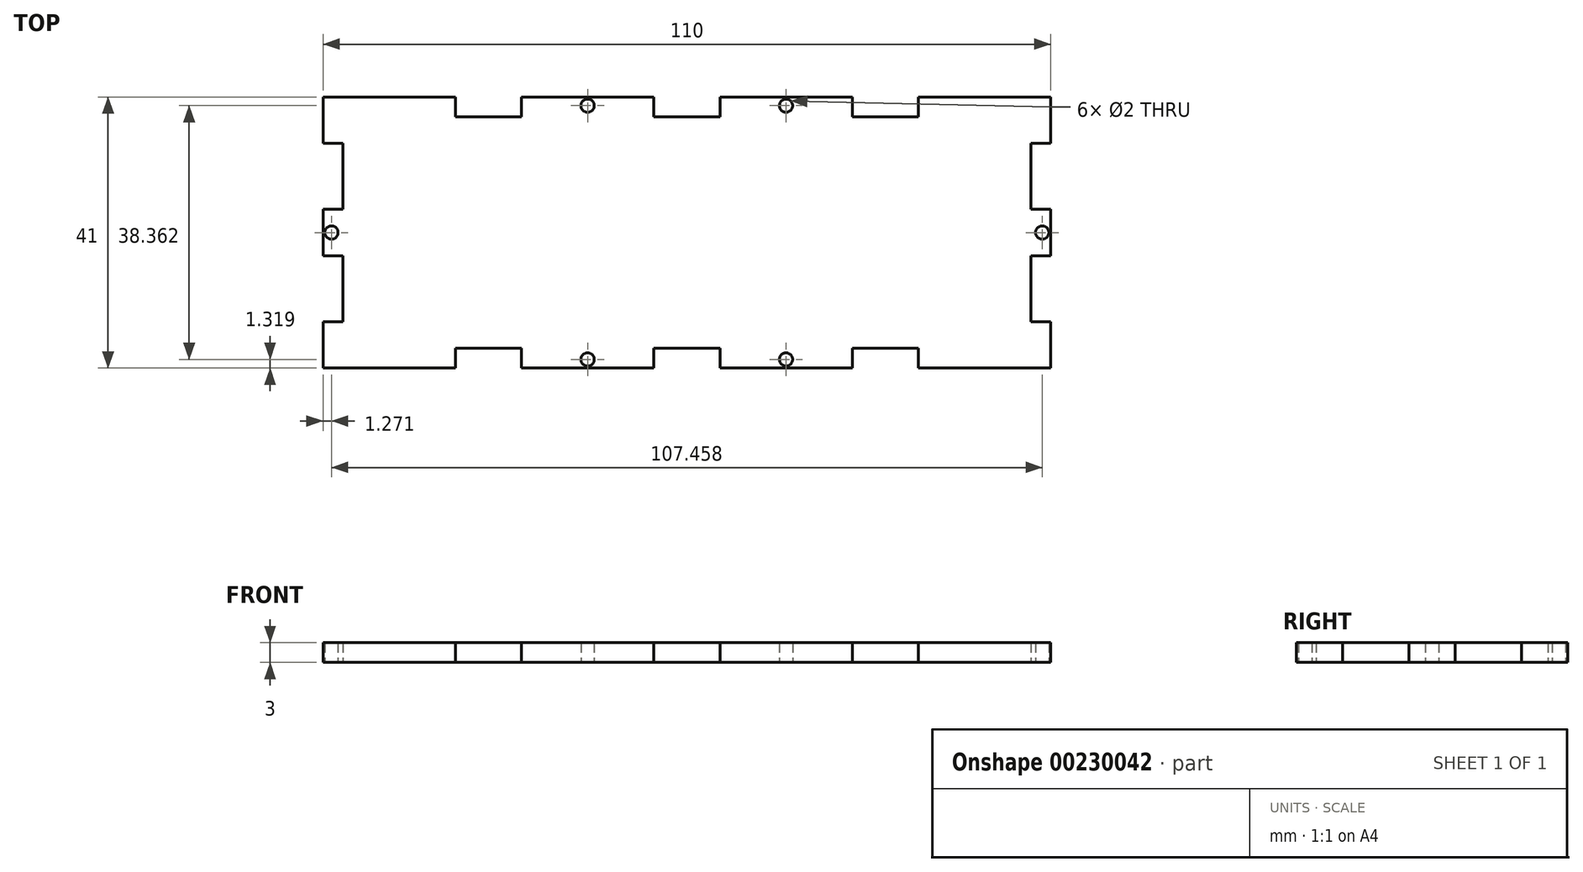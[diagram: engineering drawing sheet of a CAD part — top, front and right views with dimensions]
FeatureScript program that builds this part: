
annotation { "Feature Type Name" : "Feature", "Feature Type Description" : "" }
export const myFeature = defineFeature(function(context is Context, id is Id, definition is map)
    precondition{}
    {
        {
            var Q0;
            Q0=qCreatedBy(makeId("Top.planeOp"),FACE);
            var sketch = newSketch(context, id + "F0", { "sketchPlane" : qUnion([Q0])});
            skLineSegment(sketch, "E0", {"start": v(7.8, 0) * mm, "end": v(7.8, 7) * mm});
            skLineSegment(sketch, "E1", {"start": v(7.8, 7) * mm, "end": v(10.8, 7) * mm});
            skLineSegment(sketch, "E2", {"start": v(10.8, 7) * mm, "end": v(10.8, 17) * mm});
            skLineSegment(sketch, "E3", {"start": v(10.8, 17) * mm, "end": v(7.8, 17) * mm});
            skLineSegment(sketch, "E4", {"start": v(7.8, 17) * mm, "end": v(7.8, 24) * mm});
            skLineSegment(sketch, "E5", {"start": v(7.8, 24) * mm, "end": v(10.8, 24) * mm});
            skLineSegment(sketch, "E6", {"start": v(10.8, 24) * mm, "end": v(10.8, 34) * mm});
            skLineSegment(sketch, "E7", {"start": v(10.8, 34) * mm, "end": v(7.8, 34) * mm});
            skLineSegment(sketch, "E8", {"start": v(7.8, 34) * mm, "end": v(7.8, 41) * mm});
            skLineSegment(sketch, "E9", {"start": v(7.8, 41) * mm, "end": v(27.8, 41) * mm});
            skLineSegment(sketch, "E10", {"start": v(27.8, 41) * mm, "end": v(27.8, 38) * mm});
            skLineSegment(sketch, "E11", {"start": v(27.8, 38) * mm, "end": v(37.8, 38) * mm});
            skLineSegment(sketch, "E12", {"start": v(37.8, 38) * mm, "end": v(37.8, 41) * mm});
            skLineSegment(sketch, "E13", {"start": v(37.8, 41) * mm, "end": v(57.8, 41) * mm});
            skLineSegment(sketch, "E14", {"start": v(57.8, 41) * mm, "end": v(57.8, 38) * mm});
            skLineSegment(sketch, "E15", {"start": v(57.8, 38) * mm, "end": v(62.8, 38) * mm});
            skLineSegment(sketch, "E16", {"start": v(62.8, 38) * mm, "end": v(62.8, 0) * mm, "construction": true});
            skLineSegment(sketch, "E17", {"start": v(7.8, 20.5) * mm, "end": v(62.8, 20.5) * mm, "construction": true});
            skLineSegment(sketch, "E18.MirrorCS", {"start": v(57.8, 3) * mm, "end": v(62.8, 3) * mm});
            skLineSegment(sketch, "E19.MirrorCS", {"start": v(57.8, 0) * mm, "end": v(57.8, 3) * mm});
            skLineSegment(sketch, "E20.MirrorCS", {"start": v(37.8, 3) * mm, "end": v(37.8, 0) * mm});
            skLineSegment(sketch, "E21.MirrorCS", {"start": v(10.8, 7) * mm, "end": v(7.8, 7) * mm});
            skLineSegment(sketch, "E22.MirrorCS", {"start": v(7.8, 17) * mm, "end": v(10.8, 17) * mm});
            skLineSegment(sketch, "E23.MirrorCS", {"start": v(27.8, 0) * mm, "end": v(27.8, 3) * mm});
            skLineSegment(sketch, "E24.MirrorCS", {"start": v(37.8, 0) * mm, "end": v(57.8, 0) * mm});
            skLineSegment(sketch, "E25.MirrorCS", {"start": v(27.8, 3) * mm, "end": v(37.8, 3) * mm});
            skLineSegment(sketch, "E26.MirrorCS", {"start": v(10.8, 17) * mm, "end": v(10.8, 7) * mm});
            skLineSegment(sketch, "E27.MirrorCS", {"start": v(7.8, 7) * mm, "end": v(7.8, 0) * mm});
            skLineSegment(sketch, "E28.MirrorCS", {"start": v(7.8, 0) * mm, "end": v(27.8, 0) * mm});
            skLineSegment(sketch, "E29.MirrorCS", {"start": v(114.8, 7) * mm, "end": v(117.8, 7) * mm});
            skLineSegment(sketch, "E30.MirrorCS", {"start": v(117.8, 7) * mm, "end": v(114.8, 7) * mm});
            skLineSegment(sketch, "E31.MirrorCS", {"start": v(114.8, 17) * mm, "end": v(117.8, 17) * mm});
            skLineSegment(sketch, "E32.MirrorCS", {"start": v(117.8, 17) * mm, "end": v(114.8, 17) * mm});
            skLineSegment(sketch, "E33.MirrorCS", {"start": v(117.8, 17) * mm, "end": v(117.8, 24) * mm});
            skLineSegment(sketch, "E34.MirrorCS", {"start": v(87.8, 3) * mm, "end": v(87.8, 0) * mm});
            skLineSegment(sketch, "E35.MirrorCS", {"start": v(97.8, 0) * mm, "end": v(97.8, 3) * mm});
            skLineSegment(sketch, "E36.MirrorCS", {"start": v(87.8, 38) * mm, "end": v(87.8, 41) * mm});
            skLineSegment(sketch, "E37.MirrorCS", {"start": v(97.8, 41) * mm, "end": v(97.8, 38) * mm});
            skLineSegment(sketch, "E38.MirrorCS", {"start": v(114.8, 34) * mm, "end": v(117.8, 34) * mm});
            skLineSegment(sketch, "E39.MirrorCS", {"start": v(117.8, 24) * mm, "end": v(114.8, 24) * mm});
            skLineSegment(sketch, "E40.MirrorCS", {"start": v(67.8, 41) * mm, "end": v(67.8, 38) * mm});
            skLineSegment(sketch, "E41.MirrorCS", {"start": v(114.8, 17) * mm, "end": v(114.8, 7) * mm});
            skLineSegment(sketch, "E42.MirrorCS", {"start": v(67.8, 0) * mm, "end": v(67.8, 3) * mm});
            skLineSegment(sketch, "E43.MirrorCS", {"start": v(117.8, 0) * mm, "end": v(117.8, 7) * mm});
            skLineSegment(sketch, "E44.MirrorCS", {"start": v(114.8, 7) * mm, "end": v(114.8, 17) * mm});
            skLineSegment(sketch, "E45.MirrorCS", {"start": v(67.8, 3) * mm, "end": v(62.8, 3) * mm});
            skLineSegment(sketch, "E46.MirrorCS", {"start": v(97.8, 3) * mm, "end": v(87.8, 3) * mm});
            skLineSegment(sketch, "E47.MirrorCS", {"start": v(117.8, 7) * mm, "end": v(117.8, 0) * mm});
            skLineSegment(sketch, "E48.MirrorCS", {"start": v(97.8, 38) * mm, "end": v(87.8, 38) * mm});
            skLineSegment(sketch, "E49.MirrorCS", {"start": v(117.8, 41) * mm, "end": v(97.8, 41) * mm});
            skLineSegment(sketch, "E50.MirrorCS", {"start": v(117.8, 34) * mm, "end": v(117.8, 41) * mm});
            skLineSegment(sketch, "E51.MirrorCS", {"start": v(114.8, 24) * mm, "end": v(114.8, 34) * mm});
            skLineSegment(sketch, "E52.MirrorCS", {"start": v(67.8, 38) * mm, "end": v(62.8, 38) * mm});
            skLineSegment(sketch, "E53.MirrorCS", {"start": v(117.8, 20.5) * mm, "end": v(62.8, 20.5) * mm, "construction": true});
            skLineSegment(sketch, "E54.MirrorCS", {"start": v(87.8, 41) * mm, "end": v(67.8, 41) * mm});
            skLineSegment(sketch, "E55.MirrorCS", {"start": v(87.8, 0) * mm, "end": v(67.8, 0) * mm});
            skLineSegment(sketch, "E56.MirrorCS", {"start": v(117.8, 0) * mm, "end": v(97.8, 0) * mm});
            skCircle(sketch, "E57", {"center": v(9.08, 20.5) * mm, "radius": 1 * mm});
            skPoint(sketch, "E58", {"position": v(47.8, 0) * mm});
            skCircle(sketch, "E59", {"center": v(47.8, 1.32) * mm, "radius": 1 * mm});
            skCircle(sketch, "E60.MirrorC", {"center": v(116.54, 20.5) * mm, "radius": 1 * mm});
            skCircle(sketch, "E61.MirrorC", {"center": v(77.8, 1.32) * mm, "radius": 1 * mm});
            skCircle(sketch, "E62.MirrorC", {"center": v(47.8, 39.68) * mm, "radius": 1 * mm});
            skCircle(sketch, "E63.MirrorC", {"center": v(77.8, 39.68) * mm, "radius": 1 * mm});
            skSolve(sketch);
        }
        {
            var Q0;
            Q0=makeQuery(id+"F0.imprint","IMPRINT",FACE,{"disambiguationData":[TD([[makeQuery(id+"F0.imprint","IMPRINT",EDGE,{"derivedFrom":sQuery(id+"F0.wireOp",EDGE,"E4")}),-1.0]])]});
            extrude(context, id + "F1", {"entities" : qUnion([Q0]), "depth" : 3 * mm});
        }
    });
